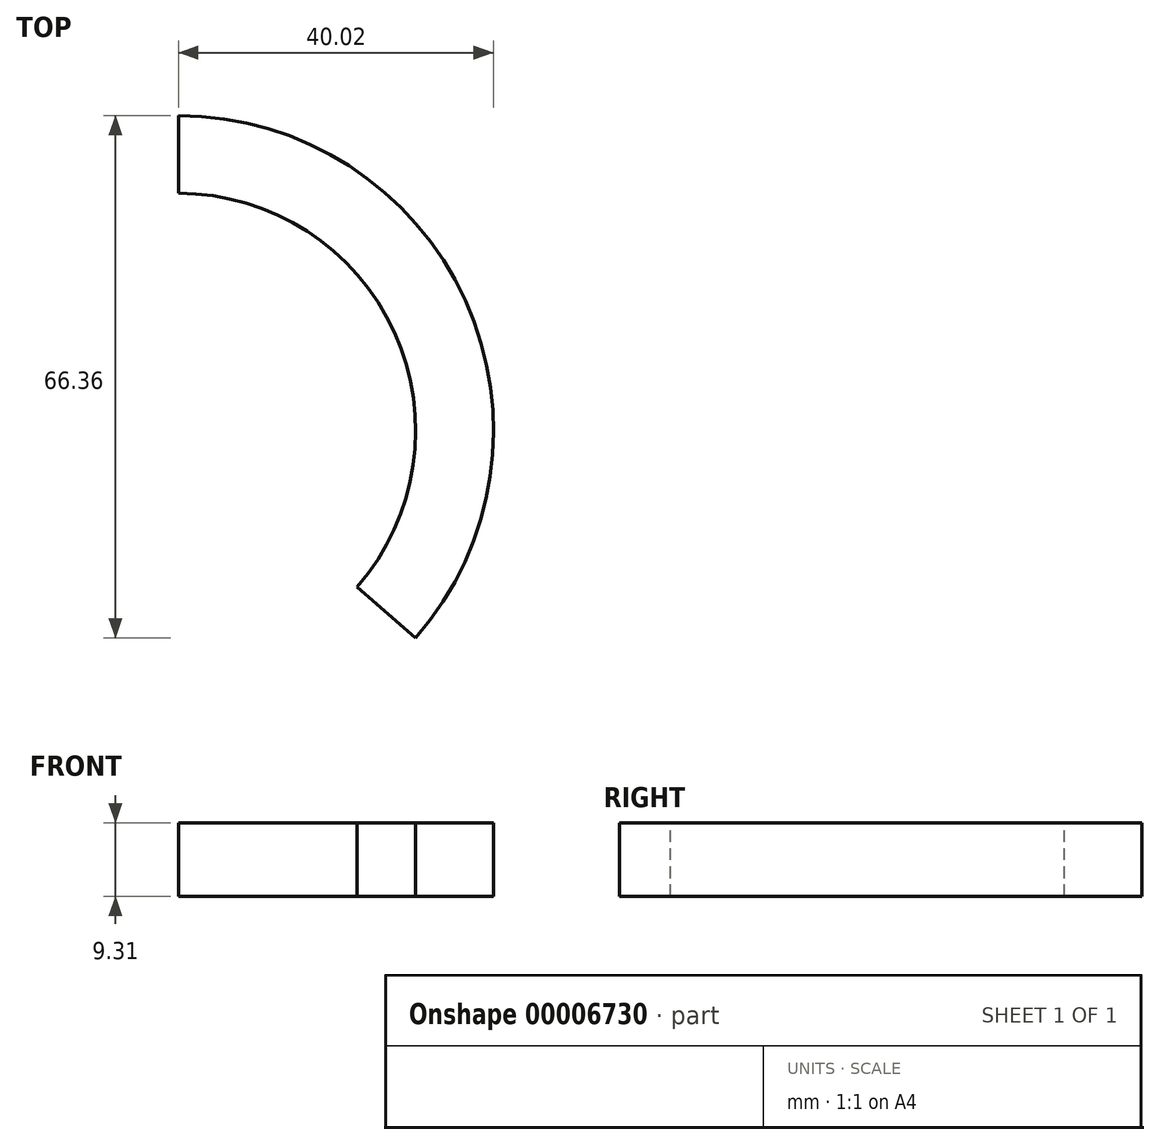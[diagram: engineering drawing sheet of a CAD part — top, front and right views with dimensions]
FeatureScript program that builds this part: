
annotation { "Feature Type Name" : "Feature", "Feature Type Description" : "" }
export const myFeature = defineFeature(function(context is Context, id is Id, definition is map)
    precondition{}
    {
        {
            var Q0;
            Q0=qCreatedBy(makeId("Top.planeOp"),FACE);
            var sketch = newSketch(context, id + "F0", { "sketchPlane" : qUnion([Q0])});
            skArc(sketch, "E0", {"start": v(45.18, -39.48) * mm, "mid": v(54.63, 24.8) * mm, "end": v(0, 60) * mm});
            skSolve(sketch);
        }
        {
            var Q0;
            Q0=qCreatedBy(makeId("Right.planeOp"),FACE);
            var sketch = newSketch(context, id + "F1", { "sketchPlane" : qUnion([Q0])});
            skLineSegment(sketch, "E1.bottom", {"start": v(30.15, 42.85) * mm, "end": v(56.47, 42.85) * mm});
            skLineSegment(sketch, "E1.top", {"start": v(30.15, 73.37) * mm, "end": v(56.47, 73.37) * mm});
            skLineSegment(sketch, "E1.left", {"start": v(30.15, 42.85) * mm, "end": v(30.15, 73.37) * mm});
            skLineSegment(sketch, "E1.right", {"start": v(56.47, 42.85) * mm, "end": v(56.47, 73.37) * mm});
            skLineSegment(sketch, "E2.bottom", {"start": v(30.15, 42.85) * mm, "end": v(40.02, 42.85) * mm});
            skLineSegment(sketch, "E2.top", {"start": v(30.15, 52.16) * mm, "end": v(40.02, 52.16) * mm});
            skLineSegment(sketch, "E2.left", {"start": v(30.15, 42.85) * mm, "end": v(30.15, 52.16) * mm});
            skLineSegment(sketch, "E2.right", {"start": v(40.02, 42.85) * mm, "end": v(40.02, 52.16) * mm});
            skSolve(sketch);
        }
        {
            var Q0;
            Q0=makeQuery(id+"F1.imprint","IMPRINT",FACE,{"disambiguationData":[TD([[makeQuery(id+"F1.imprint","IMPRINT",EDGE,{"derivedFrom":sQuery(id+"F1.wireOp",EDGE,"E1.bottom")}),1.0]])]});
            var Q1;
            Q1=sQuery(id+"F0.wireOp",EDGE,"E0");
            sweep(context, id + "F2", {"profiles" : qUnion([Q0]), "path" : qUnion([Q1])});
        }
    });
